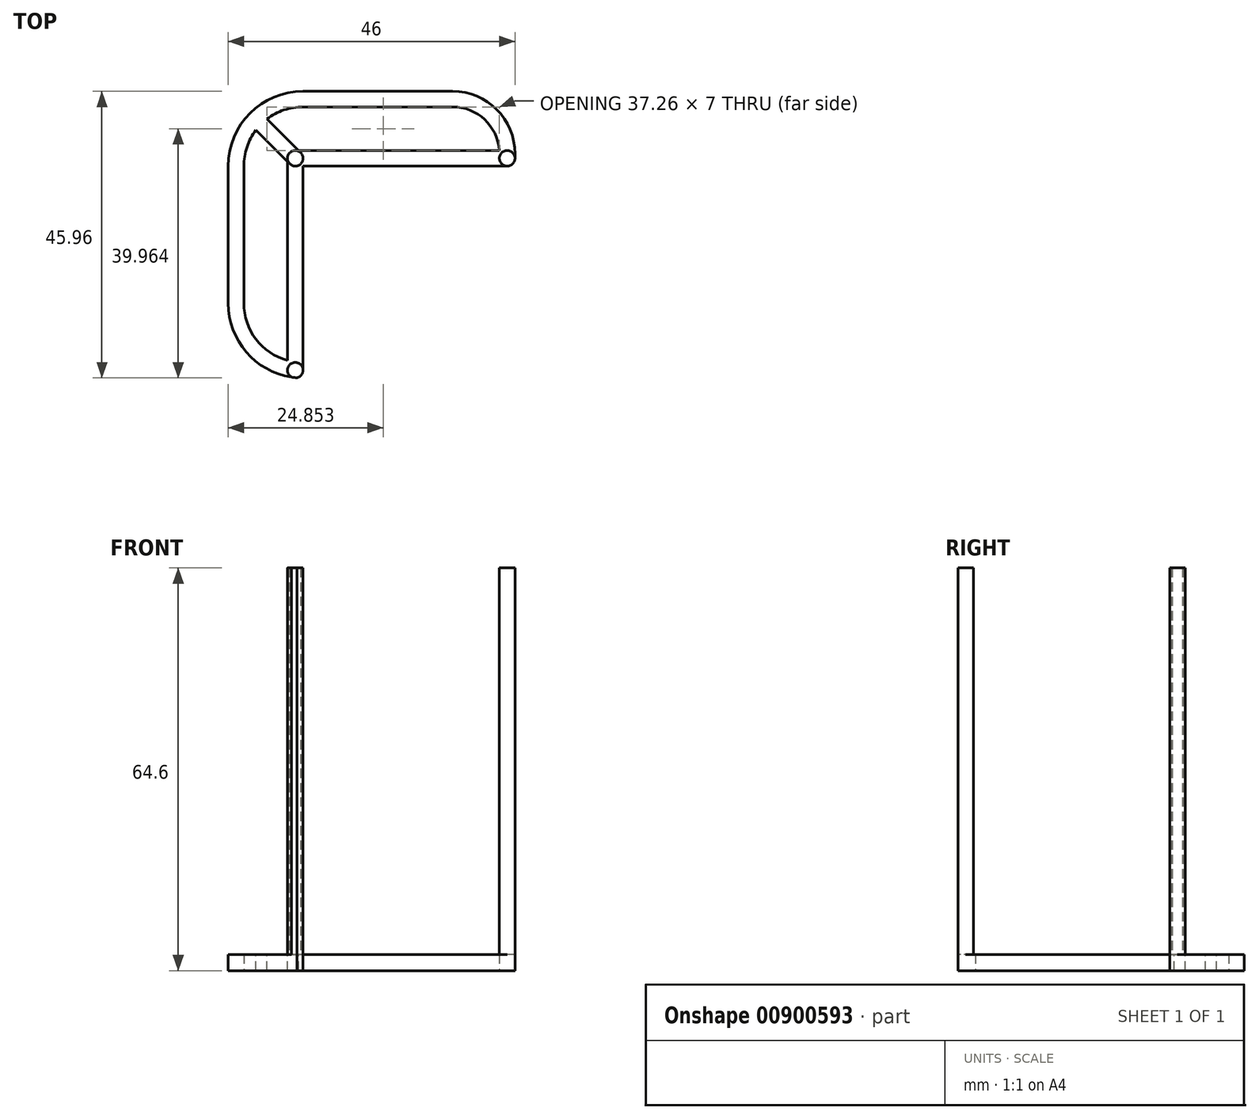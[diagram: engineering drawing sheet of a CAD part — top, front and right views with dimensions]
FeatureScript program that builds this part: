
annotation { "Feature Type Name" : "Feature", "Feature Type Description" : "" }
export const myFeature = defineFeature(function(context is Context, id is Id, definition is map)
    precondition{}
    {
        {
            var Q0;
            Q0=qCreatedBy(makeId("Top.planeOp"),FACE);
            var sketch = newSketch(context, id + "F0", { "sketchPlane" : qUnion([Q0])});
            skLineSegment(sketch, "E0.top", {"start": v(0, -25.58) * mm, "end": v(0, -25.58) * mm});
            skLineSegment(sketch, "E0.left", {"start": v(-12, 8.42) * mm, "end": v(-12, -13.58) * mm});
            skLineSegment(sketch, "E0.right", {"start": v(0, 20.42) * mm, "end": v(0, -25.58) * mm});
            skLineSegment(sketch, "E1.bottom", {"start": v(34, 8.42) * mm, "end": v(-12, 8.42) * mm});
            skLineSegment(sketch, "E1.top", {"start": v(24, 20.42) * mm, "end": v(0, 20.42) * mm});
            skLineSegment(sketch, "E1.left", {"start": v(34, 8.42) * mm, "end": v(34, 10.42) * mm});
            skPoint(sketch, "E2.third.point", {"position": v(0, 13.42) * mm});
            skPoint(sketch, "E3", {"position": v(0, 8.42) * mm});
            skPoint(sketch, "E4", {"position": v(34, 8.42) * mm});
            skPoint(sketch, "E5", {"position": v(0, -25.58) * mm});
            skPoint(sketch, "E6.visualSharp", {"position": v(34, 20.42) * mm});
            skArc(sketch, "E6.filletArc", {"start": v(34, 10.42) * mm, "mid": v(31.07, 17.5) * mm, "end": v(24, 20.42) * mm});
            skArc(sketch, "E7.filletArc", {"start": v(0, 20.42) * mm, "mid": v(-8.49, 16.9) * mm, "end": v(-12, 8.42) * mm});
            skPoint(sketch, "E8.visualSharp", {"position": v(-12, -25.58) * mm});
            skArc(sketch, "E8.filletArc", {"start": v(-12, -13.58) * mm, "mid": v(-8.49, -22.06) * mm, "end": v(0, -25.58) * mm});
            skLineSegment(sketch, "E9", {"start": v(-12, -13.58) * mm, "end": v(0, -13.58) * mm, "construction": true});
            skLineSegment(sketch, "E10", {"start": v(24, 20.42) * mm, "end": v(24, 8.42) * mm, "construction": true});
            skSolve(sketch);
        }
        {
            var Q0;
            {var subQ0=sQuery(id+"F0.wireOp",EDGE,"E1.top");var subQ1=sQuery(id+"F0.wireOp",EDGE,"E0.right");var subQ2=makeQuery(id+"F0.imprint","INTERSECT",VERTEX,{"derivedFrom":[subQ1,subQ0]});Q0=makeQuery(id+"F0.imprint","IMPRINT",FACE,{"disambiguationData":[TD([[makeQuery(id+"F0.imprint","IMPRINT",EDGE,{"disambiguationData":[TD([[subQ2,-1.0]])],"derivedFrom":subQ1}),-1.0]])]});}
            var Q1;
            {var subQ0=sQuery(id+"F0.wireOp",EDGE,"E2");var subQ1=makeQuery(id+"F0.imprint","INTERSECT",VERTEX,{"derivedFrom":[sQuery(id+"F0.wireOp",EDGE,"E1.top"),subQ0]});Q1=makeQuery(id+"F0.imprint","IMPRINT",FACE,{"disambiguationData":[TD([[makeQuery(id+"F0.imprint","IMPRINT",EDGE,{"disambiguationData":[TD([[subQ1,1.0]])],"derivedFrom":subQ0}),1.0]])]});}
            var Q2;
            {var subQ4=sQuery(id+"F0.wireOp",EDGE,"E0.right");var subQ6=sQuery(id+"F0.wireOp",EDGE,"E1.top");var subQ7=makeQuery(id+"F0.imprint","INTERSECT",VERTEX,{"derivedFrom":[subQ4,subQ6]});Q2=makeQuery(id+"F0.imprint","IMPRINT",FACE,{"disambiguationData":[TD([[makeQuery(id+"F0.imprint","IMPRINT",EDGE,{"disambiguationData":[TD([[subQ7,-1.0]])],"derivedFrom":subQ4}),1.0]])]});}
            var Q3;
            {var subQ0=sQuery(id+"F0.wireOp",EDGE,"E1.left");Q3=makeQuery(id+"F0.imprint","IMPRINT",FACE,{"disambiguationData":[TD([[makeQuery(id+"F0.imprint","IMPRINT",EDGE,{"derivedFrom":subQ0}),1.0]])]});}
            var Q4;
            {var subQ0=sQuery(id+"F0.wireOp",EDGE,"E1.left");Q4=makeQuery(id+"F0.imprint","IMPRINT",FACE,{"disambiguationData":[TD([[makeQuery(id+"F0.imprint","IMPRINT",EDGE,{"derivedFrom":subQ0}),-1.0]])]});}
            var Q5;
            {var subQ0=sQuery(id+"F0.wireOp",EDGE,"E1.bottom");var subQ1=sQuery(id+"F0.wireOp",EDGE,"E0.right");var subQ2=makeQuery(id+"F0.imprint","INTERSECT",VERTEX,{"derivedFrom":[subQ1,subQ0]});Q5=makeQuery(id+"F0.imprint","IMPRINT",FACE,{"disambiguationData":[TD([[makeQuery(id+"F0.imprint","IMPRINT",EDGE,{"disambiguationData":[TD([[subQ2,1.0]])],"derivedFrom":subQ1}),-1.0]])]});}
            var Q6;
            {var subQ0=sQuery(id+"F0.wireOp",EDGE,"E1.right");var subQ3=sQuery(id+"F0.wireOp",EDGE,"E2");var subQ5=makeQuery(id+"F0.imprint","INTERSECT",VERTEX,{"derivedFrom":[subQ0,subQ3]});Q6=makeQuery(id+"F0.imprint","IMPRINT",FACE,{"disambiguationData":[TD([[makeQuery(id+"F0.imprint","IMPRINT",EDGE,{"disambiguationData":[TD([[subQ5,-1.0]])],"derivedFrom":subQ3}),-1.0]])]});}
            var Q7;
            {var subQ1=sQuery(id+"F0.wireOp",EDGE,"E0.left");Q7=makeQuery(id+"F0.imprint","IMPRINT",FACE,{"disambiguationData":[TD([[makeQuery(id+"F0.imprint","IMPRINT",EDGE,{"derivedFrom":subQ1}),1.0]])]});}
            var Q8;
            {var subQ0=sQuery(id+"F0.wireOp",EDGE,"E0.top");Q8=makeQuery(id+"F0.imprint","IMPRINT",FACE,{"disambiguationData":[TD([[makeQuery(id+"F0.imprint","IMPRINT",EDGE,{"derivedFrom":subQ0}),1.0]])]});}
            var Q9;
            {var subQ0=sQuery(id+"F0.wireOp",EDGE,"E0.top");Q9=makeQuery(id+"F0.imprint","IMPRINT",FACE,{"disambiguationData":[TD([[makeQuery(id+"F0.imprint","IMPRINT",EDGE,{"derivedFrom":subQ0}),-1.0]])]});}
            extrude(context, id + "F1", {"entities" : qUnion([Q0, Q1, Q2, Q3, Q4, Q5, Q6, Q7, Q8, Q9]), "depth" : 2.6 * mm, "offsetDistance" : 25 * mm});
        }
        {
            var Q0;
            Q0=makeQuery(id+"F1.opExtrude","CAP_FACE",FACE,{"disambiguationData":[OSD([sQuery(id+"F0.wireOp",EDGE,"E0.left"),sQuery(id+"F0.wireOp",EDGE,"E0.right"),sQuery(id+"F0.wireOp",EDGE,"E1.bottom"),sQuery(id+"F0.wireOp",EDGE,"E1.top"),sQuery(id+"F0.wireOp",EDGE,"E1.right"),sQuery(id+"F0.wireOp",EDGE,"E2"),sQuery(id+"F0.wireOp",EDGE,"a0e31339-e725-469b-a163-157ab2d1b3e7"),sQuery(id+"F0.wireOp",EDGE,"e37d2e49-6ec8-4a07-93a9-65393287bbd5")])],"isStart":false});
            shell(context, id + "F2", {"entities" : qUnion([Q0]), "thickness" : 2.5 * mm});
        }
        {
            var Q0;
            Q0=makeQuery(id+"F2.opShell","OFFSET_FACE",FACE,{"disambiguationData":[OSD([sQuery(id+"F0.wireOp",EDGE,"E0.left"),sQuery(id+"F0.wireOp",EDGE,"E0.right"),sQuery(id+"F0.wireOp",EDGE,"E1.bottom"),sQuery(id+"F0.wireOp",EDGE,"E1.top"),sQuery(id+"F0.wireOp",EDGE,"E1.right"),sQuery(id+"F0.wireOp",EDGE,"E2"),sQuery(id+"F0.wireOp",EDGE,"a0e31339-e725-469b-a163-157ab2d1b3e7"),sQuery(id+"F0.wireOp",EDGE,"e37d2e49-6ec8-4a07-93a9-65393287bbd5")])]});
            extrude(context, id + "F3", {"entities" : qUnion([Q0]), "operationType" : NewBodyOperationType.REMOVE, "oppositeDirection" : true, "depth" : 25 * mm, "offsetDistance" : 25 * mm});
        }
        {
            var Q0;
            Q0=makeQuery(id+"F1.opExtrude","CAP_FACE",FACE,{"disambiguationData":[OSD([sQuery(id+"F0.wireOp",EDGE,"E0.left"),sQuery(id+"F0.wireOp",EDGE,"E0.right"),sQuery(id+"F0.wireOp",EDGE,"E1.bottom"),sQuery(id+"F0.wireOp",EDGE,"E1.top"),sQuery(id+"F0.wireOp",EDGE,"E1.right"),sQuery(id+"F0.wireOp",EDGE,"E2"),sQuery(id+"F0.wireOp",EDGE,"a0e31339-e725-469b-a163-157ab2d1b3e7"),sQuery(id+"F0.wireOp",EDGE,"e37d2e49-6ec8-4a07-93a9-65393287bbd5")])],"isStart":false});
            var sketch = newSketch(context, id + "F4", { "sketchPlane" : qUnion([Q0])});
            skLineSegment(sketch, "E11.bottom", {"start": v(0, 8.42) * mm, "end": v(-2.5, 8.42) * mm});
            skLineSegment(sketch, "E11.top", {"start": v(0, 10.92) * mm, "end": v(-2.5, 10.92) * mm});
            skLineSegment(sketch, "E11.left", {"start": v(0, 8.42) * mm, "end": v(0, 10.92) * mm});
            skLineSegment(sketch, "E11.right", {"start": v(-2.5, 8.42) * mm, "end": v(-2.5, 10.92) * mm});
            skLineSegment(sketch, "E12.bottom", {"start": v(34, 8.42) * mm, "end": v(31.5, 8.42) * mm});
            skLineSegment(sketch, "E12.top", {"start": v(34, 10.92) * mm, "end": v(31.5, 10.92) * mm});
            skLineSegment(sketch, "E12.left", {"start": v(34, 8.42) * mm, "end": v(34, 10.92) * mm});
            skLineSegment(sketch, "E12.right", {"start": v(31.5, 8.42) * mm, "end": v(31.5, 10.92) * mm});
            skLineSegment(sketch, "E13.bottom", {"start": v(0, -25.58) * mm, "end": v(-2.5, -25.58) * mm});
            skLineSegment(sketch, "E13.top", {"start": v(0, -23.08) * mm, "end": v(-2.5, -23.08) * mm});
            skLineSegment(sketch, "E13.left", {"start": v(0, -25.58) * mm, "end": v(0, -23.08) * mm});
            skLineSegment(sketch, "E13.right", {"start": v(-2.5, -25.58) * mm, "end": v(-2.5, -23.08) * mm});
            skCircle(sketch, "E14", {"center": v(-1.25, 9.67) * mm, "radius": 1.25 * mm});
            skPoint(sketch, "E14.centerSnap0", {"position": v(0, 9.67) * mm});
            skPoint(sketch, "E14.centerSnap1", {"position": v(-1.25, 10.92) * mm});
            skCircle(sketch, "E15", {"center": v(32.75, 9.67) * mm, "radius": 1.25 * mm});
            skPoint(sketch, "E15.centerSnap0", {"position": v(32.75, 10.92) * mm});
            skPoint(sketch, "E15.centerSnap1", {"position": v(34, 9.67) * mm});
            skCircle(sketch, "E16", {"center": v(-1.25, -24.33) * mm, "radius": 1.25 * mm});
            skPoint(sketch, "E16.centerSnap0", {"position": v(-1.25, -23.08) * mm});
            skPoint(sketch, "E16.centerSnap1", {"position": v(0, -24.33) * mm});
            skLineSegment(sketch, "E17", {"start": v(-6.19, 16.38) * mm, "end": v(-7.95, 14.61) * mm});
            skLineSegment(sketch, "E18", {"start": v(-6.19, 16.38) * mm, "end": v(-0.31, 10.5) * mm});
            skLineSegment(sketch, "E19", {"start": v(-7.95, 14.61) * mm, "end": v(-2.07, 8.73) * mm});
            skSolve(sketch);
        }
        {
            var Q0;
            {var subQ0=sQuery(id+"F4.wireOp",EDGE,"E15");var subQ1=makeQuery(id+"F4.imprint","INTERSECT",VERTEX,{"derivedFrom":[sQuery(id+"F4.wireOp",EDGE,"E12.top"),subQ0]});Q0=makeQuery(id+"F4.imprint","IMPRINT",FACE,{"disambiguationData":[TD([[makeQuery(id+"F4.imprint","IMPRINT",EDGE,{"disambiguationData":[TD([[subQ1,1.0]])],"derivedFrom":subQ0}),1.0]])]});}
            var Q1;
            {var subQ0=sQuery(id+"F4.wireOp",EDGE,"E16");var subQ1=makeQuery(id+"F4.imprint","INTERSECT",VERTEX,{"derivedFrom":[sQuery(id+"F4.wireOp",EDGE,"E13.left"),subQ0]});Q1=makeQuery(id+"F4.imprint","IMPRINT",FACE,{"disambiguationData":[TD([[makeQuery(id+"F4.imprint","IMPRINT",EDGE,{"disambiguationData":[TD([[subQ1,-1.0]])],"derivedFrom":subQ0}),1.0]])]});}
            var Q2;
            {var subQ0=sQuery(id+"F4.wireOp",EDGE,"E14");var subQ1=makeQuery(id+"F4.imprint","INTERSECT",VERTEX,{"derivedFrom":[sQuery(id+"F4.wireOp",EDGE,"E11.top"),subQ0]});Q2=makeQuery(id+"F4.imprint","IMPRINT",FACE,{"disambiguationData":[TD([[makeQuery(id+"F4.imprint","IMPRINT",EDGE,{"disambiguationData":[TD([[subQ1,1.0]])],"derivedFrom":subQ0}),1.0]])]});}
            extrude(context, id + "F5", {"entities" : qUnion([Q0, Q1, Q2]), "operationType" : NewBodyOperationType.ADD, "depth" : 62 * mm, "offsetDistance" : 25 * mm});
        }
        {
            var Q0;
            {var subQ0=sQuery(id+"F4.wireOp",EDGE,"E13.left");var subQ3=sQuery(id+"F4.wireOp",EDGE,"E16");var subQ4=makeQuery(id+"F4.imprint","INTERSECT",VERTEX,{"derivedFrom":[subQ0,subQ3]});Q0=makeQuery(id+"F4.imprint","IMPRINT",FACE,{"disambiguationData":[TD([[makeQuery(id+"F4.imprint","IMPRINT",EDGE,{"disambiguationData":[TD([[subQ4,1.0]])],"derivedFrom":subQ3}),-1.0]])]});}
            var Q1;
            {var subQ0=sQuery(id+"F4.wireOp",EDGE,"E12.left");var subQ1=sQuery(id+"F4.wireOp",EDGE,"E12.bottom");var subQ2=makeQuery(id+"F4.imprint","INTERSECT",VERTEX,{"derivedFrom":[subQ1,subQ0]});Q1=makeQuery(id+"F4.imprint","IMPRINT",FACE,{"disambiguationData":[TD([[makeQuery(id+"F4.imprint","IMPRINT",EDGE,{"disambiguationData":[TD([[subQ2,-1.0]])],"derivedFrom":subQ1}),-1.0]])]});}
            extrude(context, id + "F6", {"entities" : qUnion([Q0, Q1]), "operationType" : NewBodyOperationType.REMOVE, "oppositeDirection" : true, "depth" : 25 * mm, "offsetDistance" : 25 * mm});
        }
        {
            var Q0;
            {var subQ1=sQuery(id+"F4.wireOp",EDGE,"E11.top");var subQ8=sQuery(id+"F4.wireOp",EDGE,"E18");var subQ9=makeQuery(id+"F4.imprint","INTERSECT",VERTEX,{"derivedFrom":[subQ1,subQ8]});Q0=makeQuery(id+"F4.imprint","IMPRINT",FACE,{"disambiguationData":[TD([[makeQuery(id+"F4.imprint","IMPRINT",EDGE,{"disambiguationData":[TD([[subQ9,-1.0]])],"derivedFrom":subQ1}),-1.0]])]});}
            extrude(context, id + "F7", {"entities" : qUnion([Q0]), "operationType" : NewBodyOperationType.ADD, "oppositeDirection" : true, "depth" : 2.6 * mm, "offsetDistance" : 25 * mm});
        }
    });
